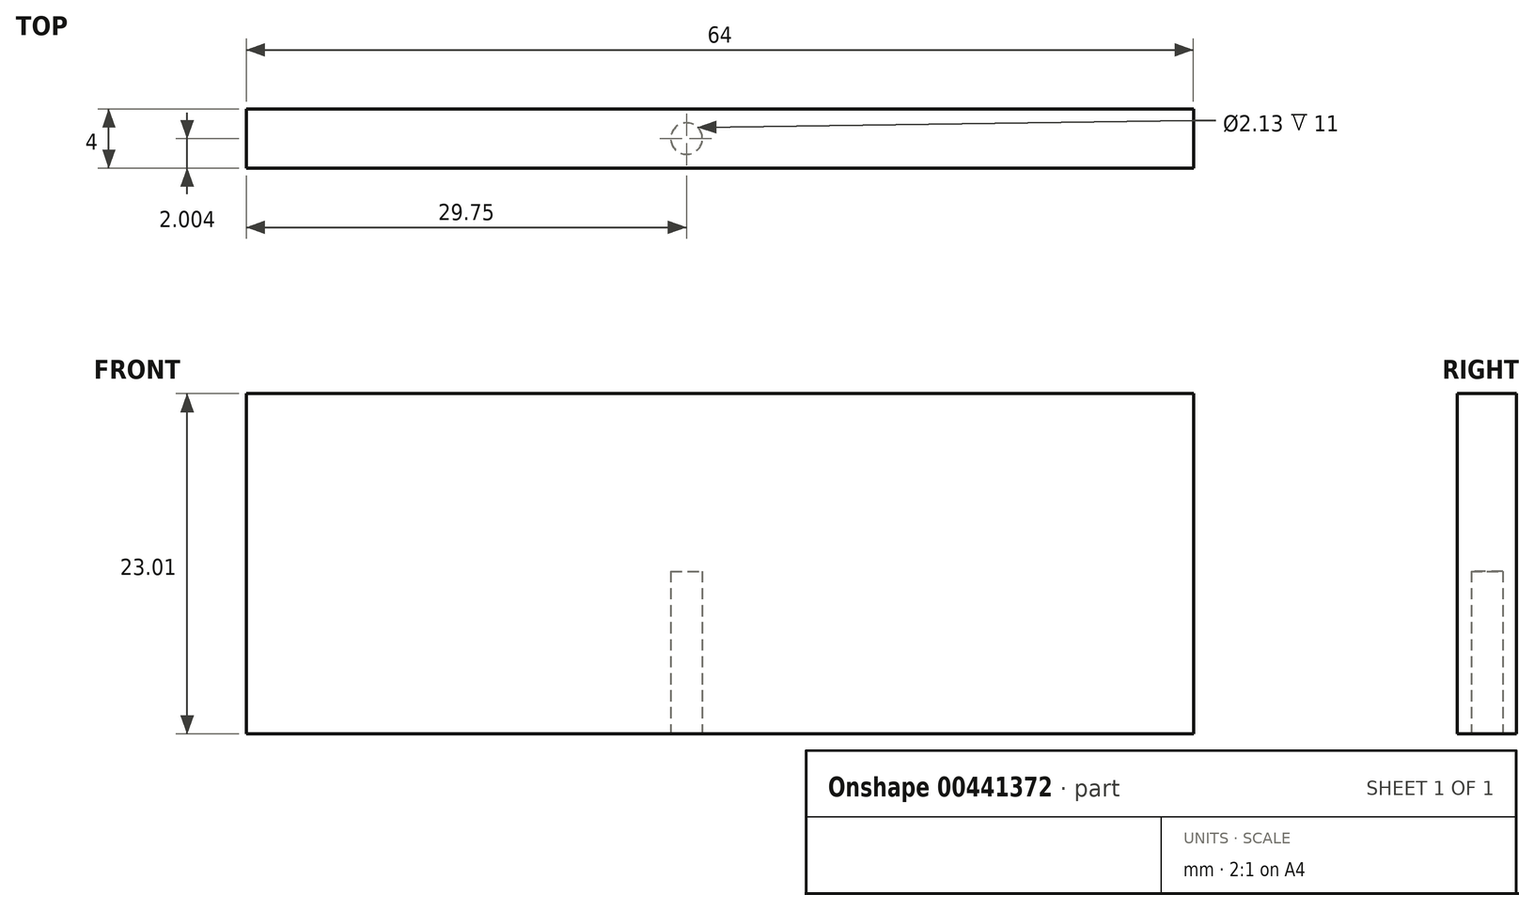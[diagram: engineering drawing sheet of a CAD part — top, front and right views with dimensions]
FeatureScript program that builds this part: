
annotation { "Feature Type Name" : "Feature", "Feature Type Description" : "" }
export const myFeature = defineFeature(function(context is Context, id is Id, definition is map)
    precondition{}
    {
        {
            var Q0;
            Q0=qCreatedBy(makeId("Front.planeOp"),FACE);
            var sketch = newSketch(context, id + "F0", { "sketchPlane" : qUnion([Q0])});
            skLineSegment(sketch, "E0.bottom", {"start": v(-29.75, 11.88) * mm, "end": v(34.25, 11.88) * mm});
            skLineSegment(sketch, "E0.top", {"start": v(-29.75, -11.13) * mm, "end": v(34.25, -11.13) * mm});
            skLineSegment(sketch, "E0.left", {"start": v(-29.75, 11.88) * mm, "end": v(-29.75, -11.13) * mm});
            skLineSegment(sketch, "E0.right", {"start": v(34.25, 11.88) * mm, "end": v(34.25, -11.13) * mm});
            skSolve(sketch);
        }
        {
            var Q0;
            Q0 = qSketchRegion(id + "F0", true);
            extrude(context, id + "F1", {"entities" : qUnion([Q0]), "depth" : 4 * mm});
        }
        {
            var Q0;
            Q0=makeQuery(id+"F1.opExtrude","SWEPT_FACE",FACE,{"disambiguationData":[OSD([sQuery(id+"F0.wireOp",EDGE,"E0.top")])]});
            var sketch = newSketch(context, id + "F2", { "sketchPlane" : qUnion([Q0])});
            skCircle(sketch, "E1", {"center": v(0, 2) * mm, "radius": 1.06 * mm});
            skSolve(sketch);
        }
        {
            var Q0;
            Q0 = qSketchRegion(id + "F2", true);
            extrude(context, id + "F3", {"entities" : qUnion([Q0]), "operationType" : NewBodyOperationType.REMOVE, "oppositeDirection" : true, "depth" : 11 * mm});
        }
    });
